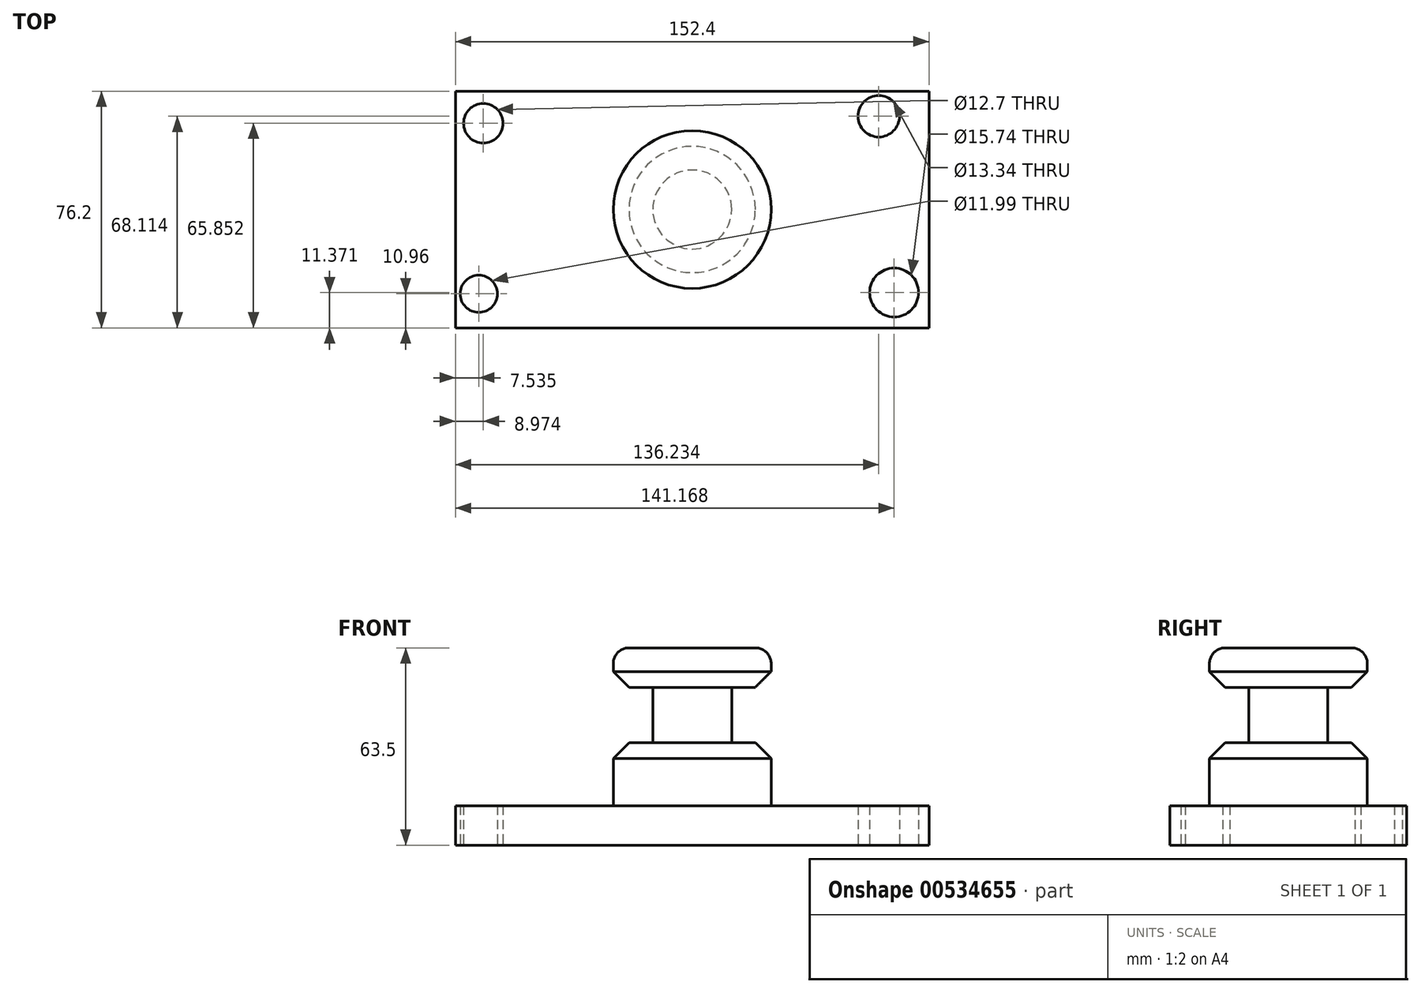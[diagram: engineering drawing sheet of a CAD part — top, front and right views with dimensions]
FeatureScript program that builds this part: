
annotation { "Feature Type Name" : "Feature", "Feature Type Description" : "" }
export const myFeature = defineFeature(function(context is Context, id is Id, definition is map)
    precondition{}
    {
        {
            var Q0;
            Q0=qCreatedBy(makeId("Top.planeOp"),FACE);
            var sketch = newSketch(context, id + "F0", { "sketchPlane" : qUnion([Q0])});
            skLineSegment(sketch, "E0.bottom", {"start": v(76.2, 38.1) * mm, "end": v(-76.2, 38.1) * mm});
            skLineSegment(sketch, "E0.top", {"start": v(76.2, -38.1) * mm, "end": v(-76.2, -38.1) * mm});
            skLineSegment(sketch, "E0.left", {"start": v(76.2, 38.1) * mm, "end": v(76.2, -38.1) * mm});
            skLineSegment(sketch, "E0.right", {"start": v(-76.2, 38.1) * mm, "end": v(-76.2, -38.1) * mm});
            skPoint(sketch, "E0.middle", {"position": v(0, 0) * mm});
            skSolve(sketch);
        }
        {
            var Q0;
            Q0=makeQuery(id+"F0.imprint","IMPRINT",FACE,{"disambiguationData":[TD([[makeQuery(id+"F0.imprint","IMPRINT",EDGE,{"derivedFrom":sQuery(id+"F0.wireOp",EDGE,"E0.bottom")}),1.0]])]});
            extrude(context, id + "F1", {"entities" : qUnion([Q0]), "depth" : 12.7 * mm, "offsetDistance" : 25.4 * mm});
        }
        {
            var Q0;
            Q0=qCreatedBy(makeId("Top.planeOp"),FACE);
            var sketch = newSketch(context, id + "F2", { "sketchPlane" : qUnion([Q0])});
            skCircle(sketch, "E1", {"center": v(-67.23, 27.75) * mm, "radius": 6.35 * mm});
            skCircle(sketch, "E2", {"center": v(-68.66, -27.14) * mm, "radius": 6 * mm});
            skCircle(sketch, "E3", {"center": v(60.03, 30.01) * mm, "radius": 6.67 * mm});
            skCircle(sketch, "E4", {"center": v(64.97, -26.73) * mm, "radius": 7.87 * mm});
            skSolve(sketch);
        }
        {
            var Q0;
            Q0 = qSketchRegion(id + "F2", true);
            extrude(context, id + "F3", {"entities" : qUnion([Q0]), "operationType" : NewBodyOperationType.REMOVE, "depth" : 12.7 * mm, "offsetDistance" : 25.4 * mm});
        }
        {
            var Q0;
            Q0=qCreatedBy(makeId("Front.planeOp"),FACE);
            var sketch = newSketch(context, id + "F4", { "sketchPlane" : qUnion([Q0])});
            skLineSegment(sketch, "E5.bottom", {"start": v(-25.4, 63.5) * mm, "end": v(0, 63.5) * mm});
            skLineSegment(sketch, "E5.top", {"start": v(-25.4, 12.7) * mm, "end": v(0, 12.7) * mm});
            skLineSegment(sketch, "E5.left", {"start": v(0, 63.5) * mm, "end": v(0, 12.7) * mm});
            skLineSegment(sketch, "E5.right", {"start": v(-25.4, 63.5) * mm, "end": v(-25.4, 12.7) * mm});
            skSolve(sketch);
        }
        {
            var Q0;
            Q0=makeQuery(id+"F4.imprint","IMPRINT",FACE,{"disambiguationData":[TD([[makeQuery(id+"F4.imprint","IMPRINT",EDGE,{"derivedFrom":sQuery(id+"F4.wireOp",EDGE,"E5.bottom")}),-1.0]])]});
            var Q1;
            Q1=sQuery(id+"F4.wireOp",EDGE,"E5.left");
            revolve(context, id + "F5", {"operationType" : NewBodyOperationType.ADD, "entities" : qUnion([Q0]), "axis" : qUnion([Q1]), "revolveType" : RevolveType.FULL});
        }
        {
            var Q0;
            Q0=qCreatedBy(makeId("Front.planeOp"),FACE);
            var sketch = newSketch(context, id + "F6", { "sketchPlane" : qUnion([Q0])});
            skLineSegment(sketch, "E6.bottom", {"start": v(12.7, 50.8) * mm, "end": v(30.48, 50.8) * mm});
            skLineSegment(sketch, "E6.top", {"start": v(12.7, 33.02) * mm, "end": v(30.48, 33.02) * mm});
            skLineSegment(sketch, "E6.left", {"start": v(12.7, 50.8) * mm, "end": v(12.7, 33.02) * mm});
            skLineSegment(sketch, "E6.right", {"start": v(30.48, 50.8) * mm, "end": v(30.48, 33.02) * mm});
            skSolve(sketch);
        }
        {
            var Q0;
            Q0=makeQuery(id+"F6.imprint","IMPRINT",FACE,{"disambiguationData":[TD([[makeQuery(id+"F6.imprint","IMPRINT",EDGE,{"derivedFrom":sQuery(id+"F6.wireOp",EDGE,"E6.bottom")}),-1.0]])]});
            var Q1;
            Q1=makeQuery(id+"F5.opRevolve","SWEPT_FACE",FACE,{"disambiguationData":[OSD([sQuery(id+"F4.wireOp",EDGE,"E5.right")])]});
            revolve(context, id + "F7", {"operationType" : NewBodyOperationType.REMOVE, "entities" : qUnion([Q0]), "axis" : qUnion([Q1]), "revolveType" : RevolveType.FULL, "oppositeDirection" : true});
        }
        {
            var Q0;
            Q0=makeQuery(id+"F5.opRevolve","SWEPT_EDGE",EDGE,{"disambiguationData":[OSD([sQuery(id+"F4.wireOp",EDGE,"E5.bottom"),sQuery(id+"F4.wireOp",EDGE,"E5.right")])]});
            var Q1;
            Q1=makeQuery(id+"F5.opRevolve","SWEPT_EDGE",EDGE,{"disambiguationData":[OSD([sQuery(id+"F4.wireOp",EDGE,"E5.top"),sQuery(id+"F4.wireOp",EDGE,"E5.right")])]});
            fillet(context, id + "F8", {"entities" : qUnion([Q0, Q1]), "radius" : 5.08 * mm, "tangentPropagation" : true, "allowEdgeOverflow" : false});
        }
        {
            var Q0;
            Q0=makeQuery(id+"F7.boolean.opBoolean","INTERSECT",EDGE,{"derivedFrom":[makeQuery(id+"F5.opRevolve","SWEPT_FACE",FACE,{"disambiguationData":[OSD([sQuery(id+"F4.wireOp",EDGE,"E5.right")])]}),makeQuery(id+"F7.opRevolve","SWEPT_FACE",FACE,{"disambiguationData":[OSD([sQuery(id+"F6.wireOp",EDGE,"E6.top")])]})]});
            var Q1;
            Q1=makeQuery(id+"F7.boolean.opBoolean","INTERSECT",EDGE,{"derivedFrom":[makeQuery(id+"F5.opRevolve","SWEPT_FACE",FACE,{"disambiguationData":[OSD([sQuery(id+"F4.wireOp",EDGE,"E5.right")])]}),makeQuery(id+"F7.opRevolve","SWEPT_FACE",FACE,{"disambiguationData":[OSD([sQuery(id+"F6.wireOp",EDGE,"E6.bottom")])]})]});
            chamfer(context, id + "F9", {"entities" : qUnion([Q0, Q1]), "width" : 5.08 * mm, "tangentPropagation" : true});
        }
    });
